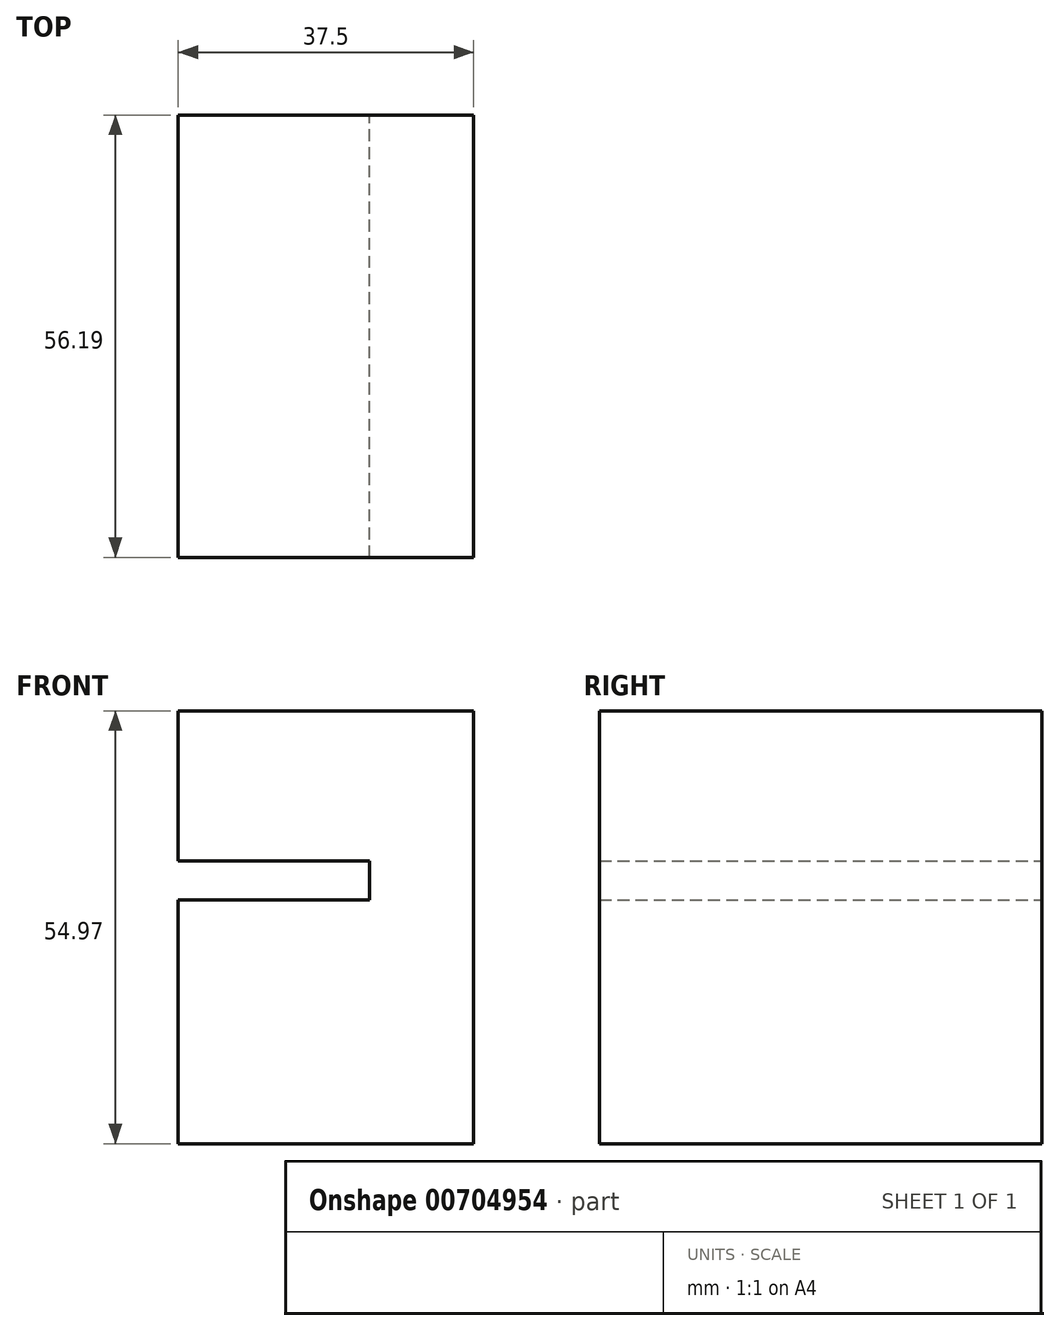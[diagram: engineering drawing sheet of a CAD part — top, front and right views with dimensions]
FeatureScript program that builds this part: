
annotation { "Feature Type Name" : "Feature", "Feature Type Description" : "" }
export const myFeature = defineFeature(function(context is Context, id is Id, definition is map)
    precondition{}
    {
        {
            var Q0;
            Q0=qCreatedBy(makeId("Front.planeOp"),FACE);
            var sketch = newSketch(context, id + "F0", { "sketchPlane" : qUnion([Q0])});
            skLineSegment(sketch, "E0.bottom", {"start": v(37.5, 35.3) * mm, "end": v(0, 35.3) * mm});
            skLineSegment(sketch, "E0.top", {"start": v(37.5, -19.68) * mm, "end": v(0, -19.68) * mm});
            skLineSegment(sketch, "E0.left", {"start": v(37.5, 35.3) * mm, "end": v(37.5, -19.68) * mm});
            skLineSegment(sketch, "E0.right", {"start": v(0, 35.3) * mm, "end": v(0, -19.68) * mm});
            skLineSegment(sketch, "E1.bottom", {"start": v(0, 16.23) * mm, "end": v(24.26, 16.23) * mm});
            skLineSegment(sketch, "E1.top", {"start": v(0, 11.27) * mm, "end": v(24.26, 11.27) * mm});
            skLineSegment(sketch, "E1.left", {"start": v(0, 16.23) * mm, "end": v(0, 11.27) * mm});
            skLineSegment(sketch, "E1.right", {"start": v(24.26, 16.23) * mm, "end": v(24.26, 11.27) * mm});
            skSolve(sketch);
        }
        {
            var Q0;
            {var subQ1=sQuery(id+"F0.wireOp",EDGE,"E0.bottom");Q0=makeQuery(id+"F0.imprint","IMPRINT",FACE,{"disambiguationData":[TD([[makeQuery(id+"F0.imprint","IMPRINT",EDGE,{"derivedFrom":subQ1}),1.0]])]});}
            extrude(context, id + "F1", {"entities" : qUnion([Q0]), "depth" : 56.2 * mm, "offsetDistance" : 25.4 * mm});
        }
    });
